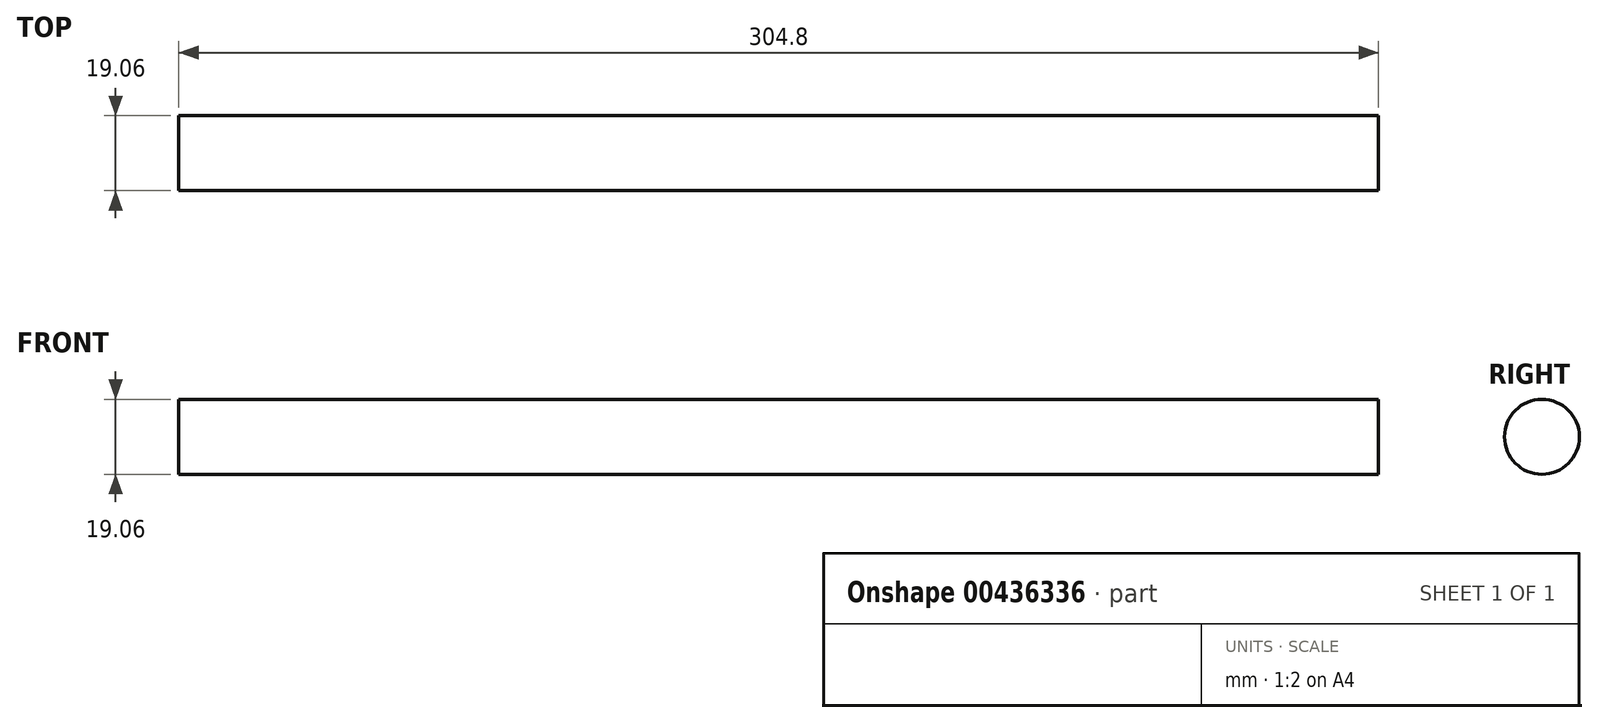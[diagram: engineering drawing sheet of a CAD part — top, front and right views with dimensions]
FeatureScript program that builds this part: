
annotation { "Feature Type Name" : "Feature", "Feature Type Description" : "" }
export const myFeature = defineFeature(function(context is Context, id is Id, definition is map)
    precondition{}
    {
        {
            var Q0;
            Q0=qCreatedBy(makeId("Right.planeOp"),FACE);
            var sketch = newSketch(context, id + "F0", { "sketchPlane" : qUnion([Q0])});
            skCircle(sketch, "E0", {"center": v(0, 0) * mm, "radius": 9.53 * mm});
            skSolve(sketch);
        }
        {
            var Q0;
            Q0 = qSketchRegion(id + "F0", true);
            extrude(context, id + "F1", {"entities" : qUnion([Q0]), "endBound" : BoundingType.SYMMETRIC, "depth" : 304.8 * mm});
        }
    });
